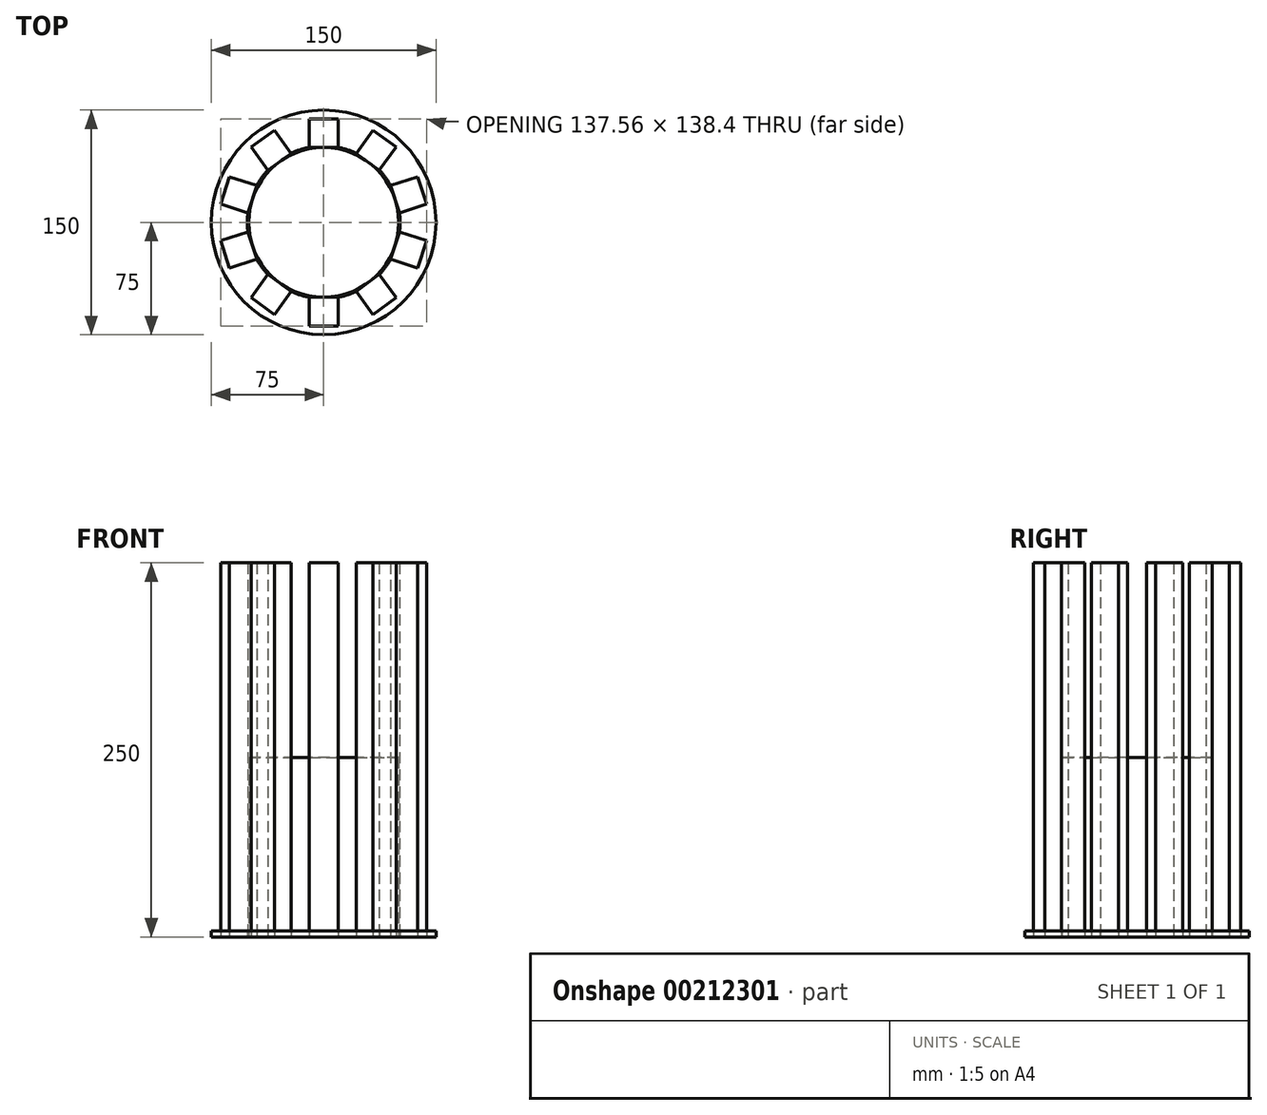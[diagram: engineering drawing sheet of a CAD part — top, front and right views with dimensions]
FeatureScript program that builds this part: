
annotation { "Feature Type Name" : "Feature", "Feature Type Description" : "" }
export const myFeature = defineFeature(function(context is Context, id is Id, definition is map)
    precondition{}
    {
        {
            var Q0;
            Q0=qCreatedBy(makeId("Top.planeOp"),FACE);
            var sketch = newSketch(context, id + "F0", { "sketchPlane" : qUnion([Q0])});
            skCircle(sketch, "E0", {"center": v(0, 0) * mm, "radius": 50 * mm});
            skLineSegment(sketch, "E1.bottom", {"start": v(-9.6, -50) * mm, "end": v(9.6, -50) * mm});
            skLineSegment(sketch, "E1.top", {"start": v(-9.6, -69.2) * mm, "end": v(9.6, -69.2) * mm});
            skLineSegment(sketch, "E1.left", {"start": v(-9.6, -50) * mm, "end": v(-9.6, -69.2) * mm});
            skLineSegment(sketch, "E1.right", {"start": v(9.6, -50) * mm, "end": v(9.6, -69.2) * mm});
            skLineSegment(sketch, "E2", {"start": v(0, 0) * mm, "end": v(0, -93.47) * mm, "construction": true});
            skPoint(sketch, "E3", {"position": v(0, -50) * mm});
            skLineSegment(sketch, "E4.1.0", {"start": v(21.62, -46.1) * mm, "end": v(37.16, -34.8) * mm});
            skLineSegment(sketch, "E4.1.1", {"start": v(37.16, -34.8) * mm, "end": v(48.44, -50.34) * mm});
            skLineSegment(sketch, "E4.1.2", {"start": v(32.9, -61.63) * mm, "end": v(48.44, -50.34) * mm});
            skLineSegment(sketch, "E4.1.3", {"start": v(21.62, -46.1) * mm, "end": v(32.9, -61.63) * mm});
            skLineSegment(sketch, "E4.2.0", {"start": v(44.59, -24.58) * mm, "end": v(50.52, -6.32) * mm});
            skLineSegment(sketch, "E4.2.1", {"start": v(50.52, -6.32) * mm, "end": v(68.78, -12.25) * mm});
            skLineSegment(sketch, "E4.2.2", {"start": v(62.85, -30.51) * mm, "end": v(68.78, -12.25) * mm});
            skLineSegment(sketch, "E4.2.3", {"start": v(44.59, -24.58) * mm, "end": v(62.85, -30.51) * mm});
            skLineSegment(sketch, "E4.3.0", {"start": v(50.52, 6.32) * mm, "end": v(44.59, 24.58) * mm});
            skLineSegment(sketch, "E4.3.1", {"start": v(44.59, 24.58) * mm, "end": v(62.85, 30.51) * mm});
            skLineSegment(sketch, "E4.3.2", {"start": v(68.78, 12.25) * mm, "end": v(62.85, 30.51) * mm});
            skLineSegment(sketch, "E4.3.3", {"start": v(50.52, 6.32) * mm, "end": v(68.78, 12.25) * mm});
            skLineSegment(sketch, "E4.4.0", {"start": v(37.16, 34.8) * mm, "end": v(21.62, 46.1) * mm});
            skLineSegment(sketch, "E4.4.1", {"start": v(21.62, 46.1) * mm, "end": v(32.9, 61.63) * mm});
            skLineSegment(sketch, "E4.4.2", {"start": v(48.44, 50.34) * mm, "end": v(32.9, 61.63) * mm});
            skLineSegment(sketch, "E4.4.3", {"start": v(37.16, 34.8) * mm, "end": v(48.44, 50.34) * mm});
            skLineSegment(sketch, "E4.5.0", {"start": v(9.6, 50) * mm, "end": v(-9.6, 50) * mm});
            skLineSegment(sketch, "E4.5.1", {"start": v(-9.6, 50) * mm, "end": v(-9.6, 69.2) * mm});
            skLineSegment(sketch, "E4.5.2", {"start": v(9.6, 69.2) * mm, "end": v(-9.6, 69.2) * mm});
            skLineSegment(sketch, "E4.5.3", {"start": v(9.6, 50) * mm, "end": v(9.6, 69.2) * mm});
            skLineSegment(sketch, "E4.6.0", {"start": v(-21.62, 46.1) * mm, "end": v(-37.16, 34.8) * mm});
            skLineSegment(sketch, "E4.6.1", {"start": v(-37.16, 34.8) * mm, "end": v(-48.44, 50.34) * mm});
            skLineSegment(sketch, "E4.6.2", {"start": v(-32.9, 61.63) * mm, "end": v(-48.44, 50.34) * mm});
            skLineSegment(sketch, "E4.6.3", {"start": v(-21.62, 46.1) * mm, "end": v(-32.9, 61.63) * mm});
            skLineSegment(sketch, "E4.7.0", {"start": v(-44.59, 24.58) * mm, "end": v(-50.52, 6.32) * mm});
            skLineSegment(sketch, "E4.7.1", {"start": v(-50.52, 6.32) * mm, "end": v(-68.78, 12.25) * mm});
            skLineSegment(sketch, "E4.7.2", {"start": v(-62.85, 30.51) * mm, "end": v(-68.78, 12.25) * mm});
            skLineSegment(sketch, "E4.7.3", {"start": v(-44.59, 24.58) * mm, "end": v(-62.85, 30.51) * mm});
            skLineSegment(sketch, "E4.8.0", {"start": v(-50.52, -6.32) * mm, "end": v(-44.59, -24.58) * mm});
            skLineSegment(sketch, "E4.8.1", {"start": v(-44.59, -24.58) * mm, "end": v(-62.85, -30.51) * mm});
            skLineSegment(sketch, "E4.8.2", {"start": v(-68.78, -12.25) * mm, "end": v(-62.85, -30.51) * mm});
            skLineSegment(sketch, "E4.8.3", {"start": v(-50.52, -6.32) * mm, "end": v(-68.78, -12.25) * mm});
            skLineSegment(sketch, "E4.9.0", {"start": v(-37.16, -34.8) * mm, "end": v(-21.62, -46.1) * mm});
            skLineSegment(sketch, "E4.9.1", {"start": v(-21.62, -46.1) * mm, "end": v(-32.9, -61.63) * mm});
            skLineSegment(sketch, "E4.9.2", {"start": v(-48.44, -50.34) * mm, "end": v(-32.9, -61.63) * mm});
            skLineSegment(sketch, "E4.9.3", {"start": v(-37.16, -34.8) * mm, "end": v(-48.44, -50.34) * mm});
            skSolve(sketch);
        }
        {
            var Q0;
            {var subQ0=sQuery(id+"F0.wireOp",EDGE,"E0");var subQ6=makeQuery(id+"F0.imprint","INTERSECT",VERTEX,{"derivedFrom":[subQ0,sQuery(id+"F0.wireOp",EDGE,"E4.4.0")]});Q0=makeQuery(id+"F0.imprint","IMPRINT",FACE,{"disambiguationData":[TD([[makeQuery(id+"F0.imprint","IMPRINT",EDGE,{"disambiguationData":[TD([[subQ6,1.0]])],"derivedFrom":subQ0}),1.0]])]});}
            extrude(context, id + "F1", {"entities" : qUnion([Q0]), "depth" : 120 * mm});
        }
        {
            var Q0;
            {var subQ0=sQuery(id+"F0.wireOp",EDGE,"E4.9.1");Q0=makeQuery(id+"F0.imprint","IMPRINT",FACE,{"disambiguationData":[TD([[makeQuery(id+"F0.imprint","IMPRINT",EDGE,{"derivedFrom":subQ0}),-1.0]])]});}
            var Q1;
            {var subQ0=sQuery(id+"F0.wireOp",EDGE,"E4.8.1");Q1=makeQuery(id+"F0.imprint","IMPRINT",FACE,{"disambiguationData":[TD([[makeQuery(id+"F0.imprint","IMPRINT",EDGE,{"derivedFrom":subQ0}),-1.0]])]});}
            var Q2;
            Q2=makeQuery(id+"F0.imprint","IMPRINT",FACE,{"disambiguationData":[TD([[makeQuery(id+"F0.imprint","IMPRINT",EDGE,{"derivedFrom":sQuery(id+"F0.wireOp",EDGE,"E1.top")}),1.0]])]});
            var Q3;
            {var subQ0=sQuery(id+"F0.wireOp",EDGE,"E4.1.1");Q3=makeQuery(id+"F0.imprint","IMPRINT",FACE,{"disambiguationData":[TD([[makeQuery(id+"F0.imprint","IMPRINT",EDGE,{"derivedFrom":subQ0}),-1.0]])]});}
            var Q4;
            {var subQ0=sQuery(id+"F0.wireOp",EDGE,"E4.2.1");Q4=makeQuery(id+"F0.imprint","IMPRINT",FACE,{"disambiguationData":[TD([[makeQuery(id+"F0.imprint","IMPRINT",EDGE,{"derivedFrom":subQ0}),-1.0]])]});}
            var Q5;
            {var subQ0=sQuery(id+"F0.wireOp",EDGE,"E4.3.1");Q5=makeQuery(id+"F0.imprint","IMPRINT",FACE,{"disambiguationData":[TD([[makeQuery(id+"F0.imprint","IMPRINT",EDGE,{"derivedFrom":subQ0}),-1.0]])]});}
            var Q6;
            {var subQ0=sQuery(id+"F0.wireOp",EDGE,"E4.4.1");Q6=makeQuery(id+"F0.imprint","IMPRINT",FACE,{"disambiguationData":[TD([[makeQuery(id+"F0.imprint","IMPRINT",EDGE,{"derivedFrom":subQ0}),-1.0]])]});}
            var Q7;
            {var subQ0=sQuery(id+"F0.wireOp",EDGE,"E4.5.1");Q7=makeQuery(id+"F0.imprint","IMPRINT",FACE,{"disambiguationData":[TD([[makeQuery(id+"F0.imprint","IMPRINT",EDGE,{"derivedFrom":subQ0}),-1.0]])]});}
            var Q8;
            {var subQ0=sQuery(id+"F0.wireOp",EDGE,"E4.6.1");Q8=makeQuery(id+"F0.imprint","IMPRINT",FACE,{"disambiguationData":[TD([[makeQuery(id+"F0.imprint","IMPRINT",EDGE,{"derivedFrom":subQ0}),-1.0]])]});}
            var Q9;
            {var subQ0=sQuery(id+"F0.wireOp",EDGE,"E4.7.1");Q9=makeQuery(id+"F0.imprint","IMPRINT",FACE,{"disambiguationData":[TD([[makeQuery(id+"F0.imprint","IMPRINT",EDGE,{"derivedFrom":subQ0}),-1.0]])]});}
            extrude(context, id + "F2", {"entities" : qUnion([Q0, Q1, Q2, Q3, Q4, Q5, Q6, Q7, Q8, Q9]), "operationType" : NewBodyOperationType.ADD, "depth" : 250 * mm});
        }
        {
            var Q0;
            Q0=qCreatedBy(makeId("Top.planeOp"),FACE);
            var sketch = newSketch(context, id + "F3", { "sketchPlane" : qUnion([Q0])});
            skLineSegment(sketch, "E5.0.0", {"start": v(0, 50) * mm, "end": v(9.6, 50) * mm});
            skLineSegment(sketch, "E5.0.1", {"start": v(9.6, 50) * mm, "end": v(9.6, 69.2) * mm});
            skLineSegment(sketch, "E5.0.2", {"start": v(9.6, 69.2) * mm, "end": v(-9.6, 69.2) * mm});
            skLineSegment(sketch, "E5.0.3", {"start": v(-9.6, 69.2) * mm, "end": v(-9.6, 50) * mm});
            skLineSegment(sketch, "E5.0.4", {"start": v(-9.6, 50) * mm, "end": v(0, 50) * mm});
            skLineSegment(sketch, "E5.1.0", {"start": v(-29.39, 40.45) * mm, "end": v(-21.62, 46.1) * mm});
            skLineSegment(sketch, "E5.1.2", {"start": v(-32.9, 61.63) * mm, "end": v(-48.44, 50.34) * mm});
            skLineSegment(sketch, "E5.1.3", {"start": v(-48.44, 50.34) * mm, "end": v(-37.16, 34.8) * mm});
            skLineSegment(sketch, "E5.1.4", {"start": v(-37.16, 34.8) * mm, "end": v(-29.39, 40.45) * mm});
            skLineSegment(sketch, "E5.2.0", {"start": v(-47.55, 15.45) * mm, "end": v(-44.59, 24.58) * mm});
            skLineSegment(sketch, "E5.2.1", {"start": v(-44.59, 24.58) * mm, "end": v(-62.85, 30.51) * mm});
            skLineSegment(sketch, "E5.2.2", {"start": v(-62.85, 30.51) * mm, "end": v(-68.78, 12.25) * mm});
            skLineSegment(sketch, "E5.2.3", {"start": v(-68.78, 12.25) * mm, "end": v(-50.52, 6.32) * mm});
            skLineSegment(sketch, "E5.2.4", {"start": v(-50.52, 6.32) * mm, "end": v(-47.55, 15.45) * mm});
            skLineSegment(sketch, "E5.3.0", {"start": v(-47.55, -15.45) * mm, "end": v(-50.52, -6.32) * mm});
            skLineSegment(sketch, "E5.3.1", {"start": v(-50.52, -6.32) * mm, "end": v(-68.78, -12.25) * mm});
            skLineSegment(sketch, "E5.3.2", {"start": v(-68.78, -12.25) * mm, "end": v(-62.85, -30.51) * mm});
            skLineSegment(sketch, "E5.3.3", {"start": v(-62.85, -30.51) * mm, "end": v(-44.59, -24.58) * mm});
            skLineSegment(sketch, "E5.3.4", {"start": v(-44.59, -24.58) * mm, "end": v(-47.55, -15.45) * mm});
            skLineSegment(sketch, "E5.4.0", {"start": v(-29.39, -40.45) * mm, "end": v(-37.16, -34.8) * mm});
            skLineSegment(sketch, "E5.4.1", {"start": v(-37.16, -34.8) * mm, "end": v(-48.44, -50.34) * mm});
            skLineSegment(sketch, "E5.4.2", {"start": v(-48.44, -50.34) * mm, "end": v(-32.9, -61.63) * mm});
            skLineSegment(sketch, "E5.4.3", {"start": v(-32.9, -61.63) * mm, "end": v(-21.62, -46.1) * mm});
            skLineSegment(sketch, "E5.4.4", {"start": v(-21.62, -46.1) * mm, "end": v(-29.39, -40.45) * mm});
            skLineSegment(sketch, "E5.5.0", {"start": v(-9.6, -50) * mm, "end": v(-9.6, -69.2) * mm});
            skLineSegment(sketch, "E5.5.1", {"start": v(-9.6, -69.2) * mm, "end": v(9.6, -69.2) * mm});
            skLineSegment(sketch, "E5.5.2", {"start": v(9.6, -69.2) * mm, "end": v(9.6, -50) * mm});
            skLineSegment(sketch, "E5.5.3", {"start": v(9.6, -50) * mm, "end": v(0, -50) * mm});
            skLineSegment(sketch, "E5.5.4", {"start": v(0, -50) * mm, "end": v(-9.6, -50) * mm});
            skLineSegment(sketch, "E5.6.0", {"start": v(29.39, -40.45) * mm, "end": v(21.62, -46.1) * mm});
            skLineSegment(sketch, "E5.6.1", {"start": v(21.62, -46.1) * mm, "end": v(32.9, -61.63) * mm});
            skLineSegment(sketch, "E5.6.2", {"start": v(32.9, -61.63) * mm, "end": v(48.44, -50.34) * mm});
            skLineSegment(sketch, "E5.6.3", {"start": v(48.44, -50.34) * mm, "end": v(37.16, -34.8) * mm});
            skLineSegment(sketch, "E5.6.4", {"start": v(37.16, -34.8) * mm, "end": v(29.39, -40.45) * mm});
            skLineSegment(sketch, "E5.7.0", {"start": v(47.55, -15.45) * mm, "end": v(44.59, -24.58) * mm});
            skLineSegment(sketch, "E5.7.1", {"start": v(44.59, -24.58) * mm, "end": v(62.85, -30.51) * mm});
            skLineSegment(sketch, "E5.7.2", {"start": v(62.85, -30.51) * mm, "end": v(68.78, -12.25) * mm});
            skLineSegment(sketch, "E5.7.3", {"start": v(68.78, -12.25) * mm, "end": v(50.52, -6.32) * mm});
            skLineSegment(sketch, "E5.7.4", {"start": v(50.52, -6.32) * mm, "end": v(47.55, -15.45) * mm});
            skLineSegment(sketch, "E5.8.0", {"start": v(47.55, 15.45) * mm, "end": v(50.52, 6.32) * mm});
            skLineSegment(sketch, "E5.8.1", {"start": v(50.52, 6.32) * mm, "end": v(68.78, 12.25) * mm});
            skLineSegment(sketch, "E5.8.2", {"start": v(68.78, 12.25) * mm, "end": v(62.85, 30.51) * mm});
            skLineSegment(sketch, "E5.8.3", {"start": v(62.85, 30.51) * mm, "end": v(44.59, 24.58) * mm});
            skLineSegment(sketch, "E5.8.4", {"start": v(44.59, 24.58) * mm, "end": v(47.55, 15.45) * mm});
            skLineSegment(sketch, "E5.9.0", {"start": v(29.39, 40.45) * mm, "end": v(37.16, 34.8) * mm});
            skLineSegment(sketch, "E5.9.1", {"start": v(37.16, 34.8) * mm, "end": v(48.44, 50.34) * mm});
            skLineSegment(sketch, "E5.9.2", {"start": v(48.44, 50.34) * mm, "end": v(32.9, 61.63) * mm});
            skLineSegment(sketch, "E5.9.3", {"start": v(32.9, 61.63) * mm, "end": v(21.62, 46.1) * mm});
            skLineSegment(sketch, "E5.9.4", {"start": v(21.62, 46.1) * mm, "end": v(29.39, 40.45) * mm});
            skArc(sketch, "E5.10.0", {"start": v(47.55, -15.45) * mm, "mid": v(50, 0) * mm, "end": v(47.55, 15.45) * mm});
            skArc(sketch, "E5.10.1", {"start": v(47.55, 15.45) * mm, "mid": v(40.45, 29.39) * mm, "end": v(29.39, 40.45) * mm});
            skArc(sketch, "E5.10.2", {"start": v(29.39, 40.45) * mm, "mid": v(15.45, 47.55) * mm, "end": v(0, 50) * mm});
            skArc(sketch, "E5.10.3", {"start": v(0, 50) * mm, "mid": v(-15.45, 47.55) * mm, "end": v(-29.39, 40.45) * mm});
            skArc(sketch, "E5.10.4", {"start": v(-29.39, 40.45) * mm, "mid": v(-40.45, 29.39) * mm, "end": v(-47.55, 15.45) * mm});
            skArc(sketch, "E5.10.5", {"start": v(-47.55, 15.45) * mm, "mid": v(-50, 0) * mm, "end": v(-47.55, -15.45) * mm});
            skArc(sketch, "E5.10.6", {"start": v(-47.55, -15.45) * mm, "mid": v(-40.45, -29.39) * mm, "end": v(-29.39, -40.45) * mm});
            skArc(sketch, "E5.10.7", {"start": v(-29.39, -40.45) * mm, "mid": v(-15.45, -47.55) * mm, "end": v(0, -50) * mm});
            skArc(sketch, "E5.10.8", {"start": v(0, -50) * mm, "mid": v(15.45, -47.55) * mm, "end": v(29.39, -40.45) * mm});
            skArc(sketch, "E5.10.9", {"start": v(29.39, -40.45) * mm, "mid": v(40.45, -29.39) * mm, "end": v(47.55, -15.45) * mm});
            skCircle(sketch, "E6", {"center": v(0, 0) * mm, "radius": 75 * mm});
            skLineSegment(sketch, "E7.0", {"start": v(-21.62, 46.1) * mm, "end": v(-32.9, 61.63) * mm});
            skCircle(sketch, "E8", {"center": v(0, 0) * mm, "radius": 51 * mm});
            skSolve(sketch);
        }
        {
            var Q0;
            {var subQ26=sQuery(id+"F3.wireOp",EDGE,"E5.0.2");Q0=makeQuery(id+"F3.imprint","IMPRINT",FACE,{"disambiguationData":[TD([[makeQuery(id+"F3.imprint","IMPRINT",EDGE,{"derivedFrom":subQ26}),-1.0]])]});}
            extrude(context, id + "F4", {"entities" : qUnion([Q0]), "depth" : 4 * mm});
        }
    });
